FCSTD DOCUMENT  (FreeCAD 0.21R33668 +26 (Git))
Label: encoder_edge
License: All rights reserved
LicenseURL: https://en.wikipedia.org/wiki/All_rights_reserved
objects: Sketcher::SketchObject×1
note: 1 computed .brp shape members not serialized (recipe doc carries the construction recipe); baked Part::Feature solids carry a one-line shape summary decoded from their .brp

FEATURE [Sketcher::SketchObject] Sketch
  FullyConstrained = true
  sketch-geometry (10):
    g0: LineSegment StartX=-15.3895 StartY=0.921038 StartZ=0 EndX=-1.94736 EndY=6.60519 EndZ=0
    g1: LineSegment StartX=1.94736 StartY=6.60519 StartZ=0 EndX=15.3895 EndY=0.921038 EndZ=0
    g2: LineSegment StartX=15.3895 StartY=-0.921038 StartZ=0 EndX=1.94736 EndY=-6.60519 EndZ=0
    g3: LineSegment StartX=-1.94736 StartY=-6.60519 StartZ=0 EndX=-15.3895 EndY=-0.921038 EndZ=0
    g4: ArcOfCircle CenterX=-15 CenterY=0 CenterZ=0 NormalX=0 NormalY=0 NormalZ=1 AngleXU=0 Radius=1 StartAngle=1.97085 EndAngle=4.31233
    g5: ArcOfCircle CenterX=15 CenterY=0 CenterZ=0 NormalX=0 NormalY=0 NormalZ=1 AngleXU=0 Radius=1 StartAngle=5.11245 EndAngle=7.45392
    g6: ArcOfCircle CenterX=0 CenterY=-2 CenterZ=0 NormalX=0 NormalY=0 NormalZ=1 AngleXU=0 Radius=5 StartAngle=4.31233 EndAngle=5.11245
    g7: ArcOfCircle CenterX=0 CenterY=2 CenterZ=0 NormalX=0 NormalY=0 NormalZ=1 AngleXU=0 Radius=5 StartAngle=1.17074 EndAngle=1.97085
    g8: Circle CenterX=-10 CenterY=0 CenterZ=0 NormalX=0 NormalY=0 NormalZ=1 AngleXU=0 Radius=2.2
    g9: Circle CenterX=10 CenterY=0 CenterZ=0 NormalX=0 NormalY=0 NormalZ=1 AngleXU=0 Radius=2.2
  constraints (25):
    c: Equal(g1,g2)
    c: Equal(g0,g1)
    c: Tangent(g0,g4) = 1.5708
    c: Tangent(g3,g4) = 1.5708
    c: Tangent(g1,g5) = 1.5708
    c: Tangent(g2,g5) = 1.5708
    c: Tangent(g3,g6) = 1.5708
    c: Tangent(g2,g6) = 1.5708
    c: Tangent(g1,g7) = 1.5708
    c: Tangent(g0,g7) = 1.5708
    c: Diameter(g5) = 2
    c: Diameter(g4) = 2
    c: PointOnObject(g4,g-1)
    c: PointOnObject(g5,g-1)
    c: Diameter(g7) = 10
    c: DistanceX(g4,g5) = 30
    c: Diameter(g6) = 10
    c: PointOnObject(g7,g-2)
    c: PointOnObject(g6,g-2)
    c: DistanceY(g6,g7) = 4
    c: PointOnObject(g8,g-1)
    c: Equal(g8,g9)
    c: Diameter(g8) = 4.4
    c: Symmetric(g8,g9,g-1)
    c: DistanceX(g8,g-1) = 10
